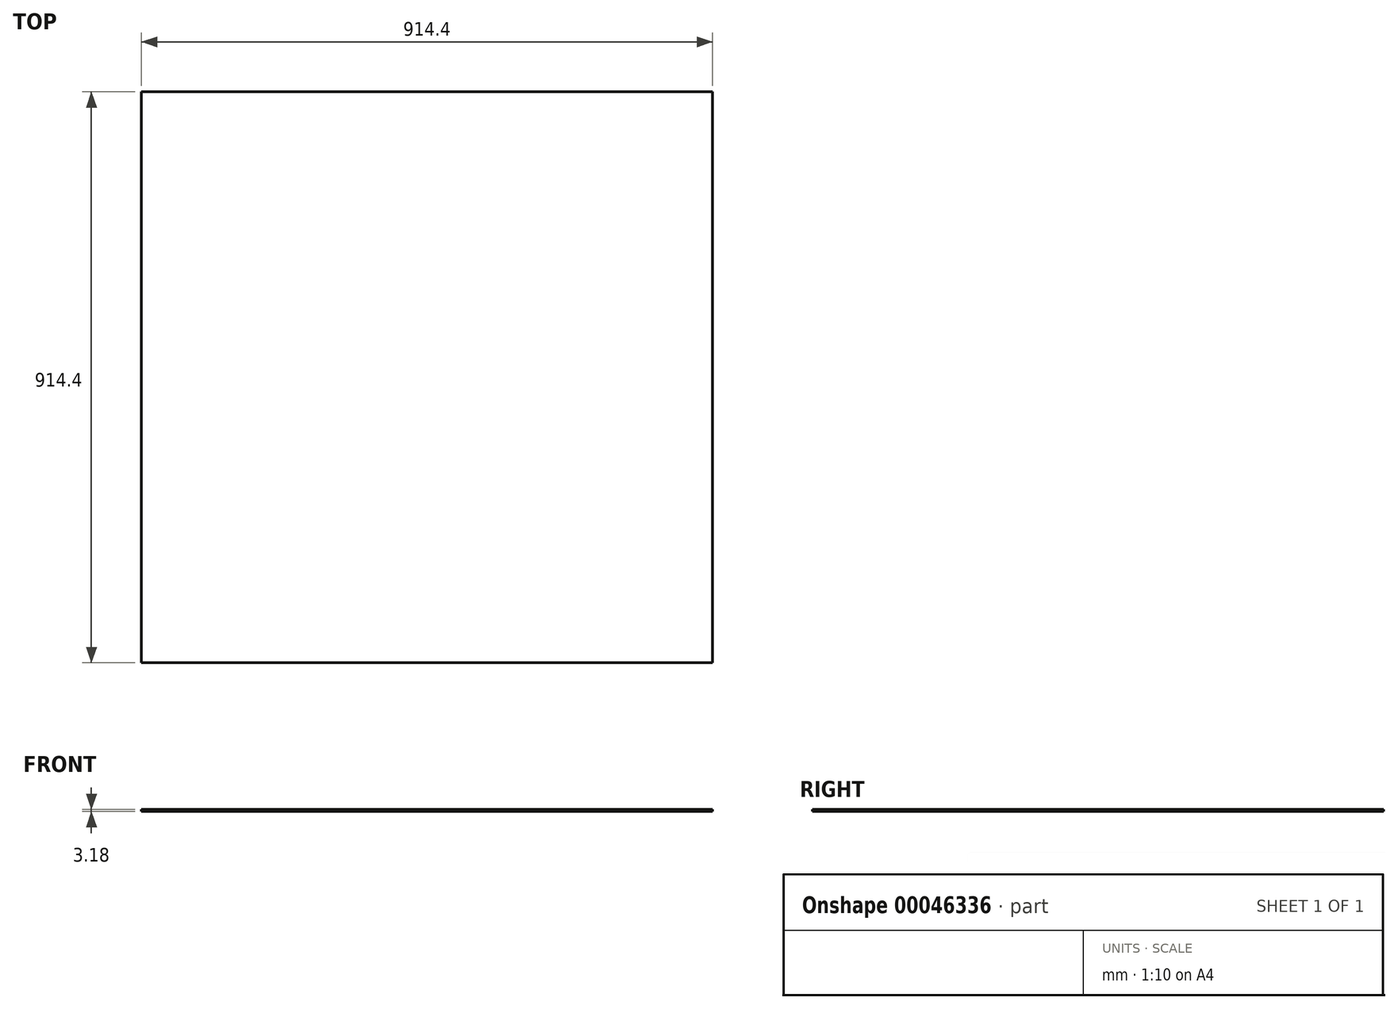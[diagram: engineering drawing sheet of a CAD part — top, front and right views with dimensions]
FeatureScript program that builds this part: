
annotation { "Feature Type Name" : "Feature", "Feature Type Description" : "" }
export const myFeature = defineFeature(function(context is Context, id is Id, definition is map)
    precondition{}
    {
        {
            var Q0;
            Q0=qCreatedBy(makeId("Top.planeOp"),FACE);
            var sketch = newSketch(context, id + "F0", { "sketchPlane" : qUnion([Q0])});
            skLineSegment(sketch, "E0.rect.bottom", {"start": v(457.2, 457.2) * mm, "end": v(-457.2, 457.2) * mm});
            skLineSegment(sketch, "E0.rect.top", {"start": v(457.2, -457.2) * mm, "end": v(-457.2, -457.2) * mm});
            skLineSegment(sketch, "E0.rect.left", {"start": v(457.2, 457.2) * mm, "end": v(457.2, -457.2) * mm});
            skLineSegment(sketch, "E0.rect.right", {"start": v(-457.2, 457.2) * mm, "end": v(-457.2, -457.2) * mm});
            skPoint(sketch, "E0.rect.middle", {"position": v(0, 0) * mm});
            skSolve(sketch);
        }
        {
            var Q0;
            Q0=makeQuery(id+"F0.imprint","IMPRINT",FACE,{"disambiguationData":[TD([[makeQuery(id+"F0.imprint","IMPRINT",EDGE,{"derivedFrom":sQuery(id+"F0.wireOp",EDGE,"E0.rect.bottom")}),1.0]])]});
            extrude(context, id + "F1", {"entities" : qUnion([Q0]), "endBound" : BoundingType.SYMMETRIC, "depth" : 3.17 * mm});
        }
    });
